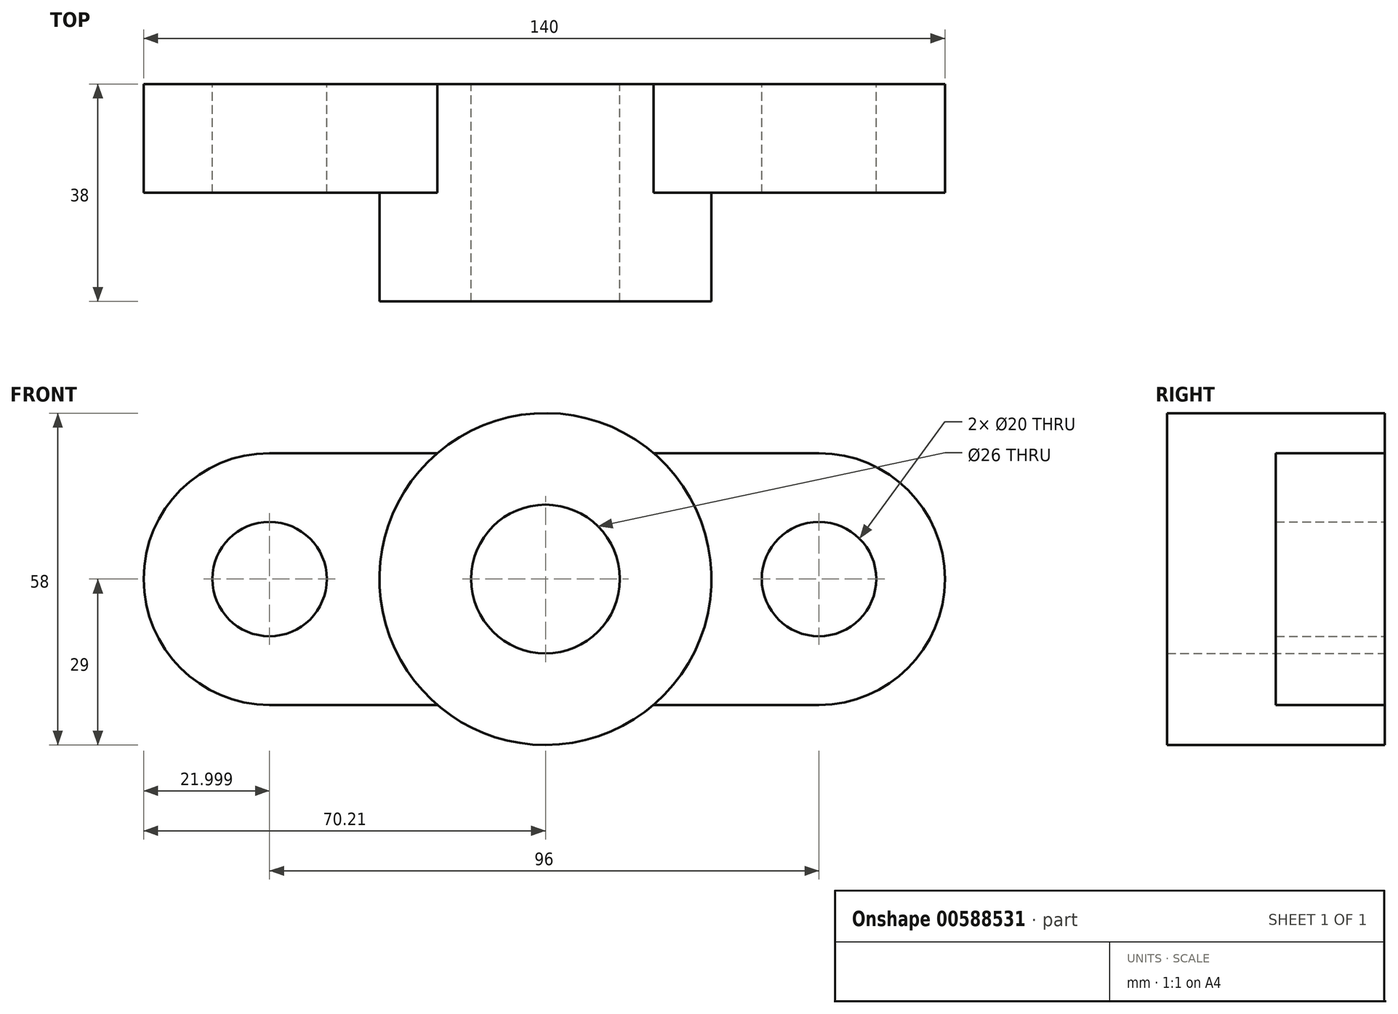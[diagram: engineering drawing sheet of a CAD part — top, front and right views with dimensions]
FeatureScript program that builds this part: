
annotation { "Feature Type Name" : "Feature", "Feature Type Description" : "" }
export const myFeature = defineFeature(function(context is Context, id is Id, definition is map)
    precondition{}
    {
        {
            var Q0;
            Q0=qCreatedBy(makeId("Front.planeOp"),FACE);
            var sketch = newSketch(context, id + "F0", { "sketchPlane" : qUnion([Q0])});
            skCircle(sketch, "E0", {"center": v(0, 0) * mm, "radius": 29 * mm});
            skCircle(sketch, "E1", {"center": v(0, 0) * mm, "radius": 13 * mm});
            skCircle(sketch, "E2", {"center": v(-48.21, 0) * mm, "radius": 10 * mm});
            skCircle(sketch, "E3", {"center": v(47.79, 0) * mm, "radius": 10 * mm});
            skLineSegment(sketch, "E4", {"start": v(-48.21, -22) * mm, "end": v(-18.9, -22) * mm});
            skLineSegment(sketch, "E5", {"start": v(47.79, 22) * mm, "end": v(18.9, 22) * mm});
            skLineSegment(sketch, "E6.trimOffspring", {"start": v(-18.9, 22) * mm, "end": v(-48.21, 22) * mm});
            skLineSegment(sketch, "E7.trimOffspring", {"start": v(18.9, -22) * mm, "end": v(47.79, -22) * mm});
            skArc(sketch, "E8", {"start": v(27.63, -8.8) * mm, "mid": v(69.79, 0) * mm, "end": v(27.63, 8.8) * mm});
            skArc(sketch, "E9", {"start": v(-27.8, 8.23) * mm, "mid": v(-70.21, 0) * mm, "end": v(-27.8, -8.23) * mm});
            skSolve(sketch);
        }
        {
            var Q0;
            Q0 = qSketchRegion(id + "F0", true);
            extrude(context, id + "F1", {"entities" : qUnion([Q0]), "depth" : 19 * mm, "offsetDistance" : 25 * mm});
        }
        {
            var Q0;
            Q0=makeQuery(id+"F0.imprint","IMPRINT",FACE,{"disambiguationData":[TD([[makeQuery(id+"F0.imprint","IMPRINT",EDGE,{"derivedFrom":sQuery(id+"F0.wireOp",EDGE,"E1")}),-1.0]])]});
            extrude(context, id + "F2", {"entities" : qUnion([Q0]), "operationType" : NewBodyOperationType.ADD, "depth" : 38 * mm, "offsetDistance" : 25 * mm});
        }
    });
